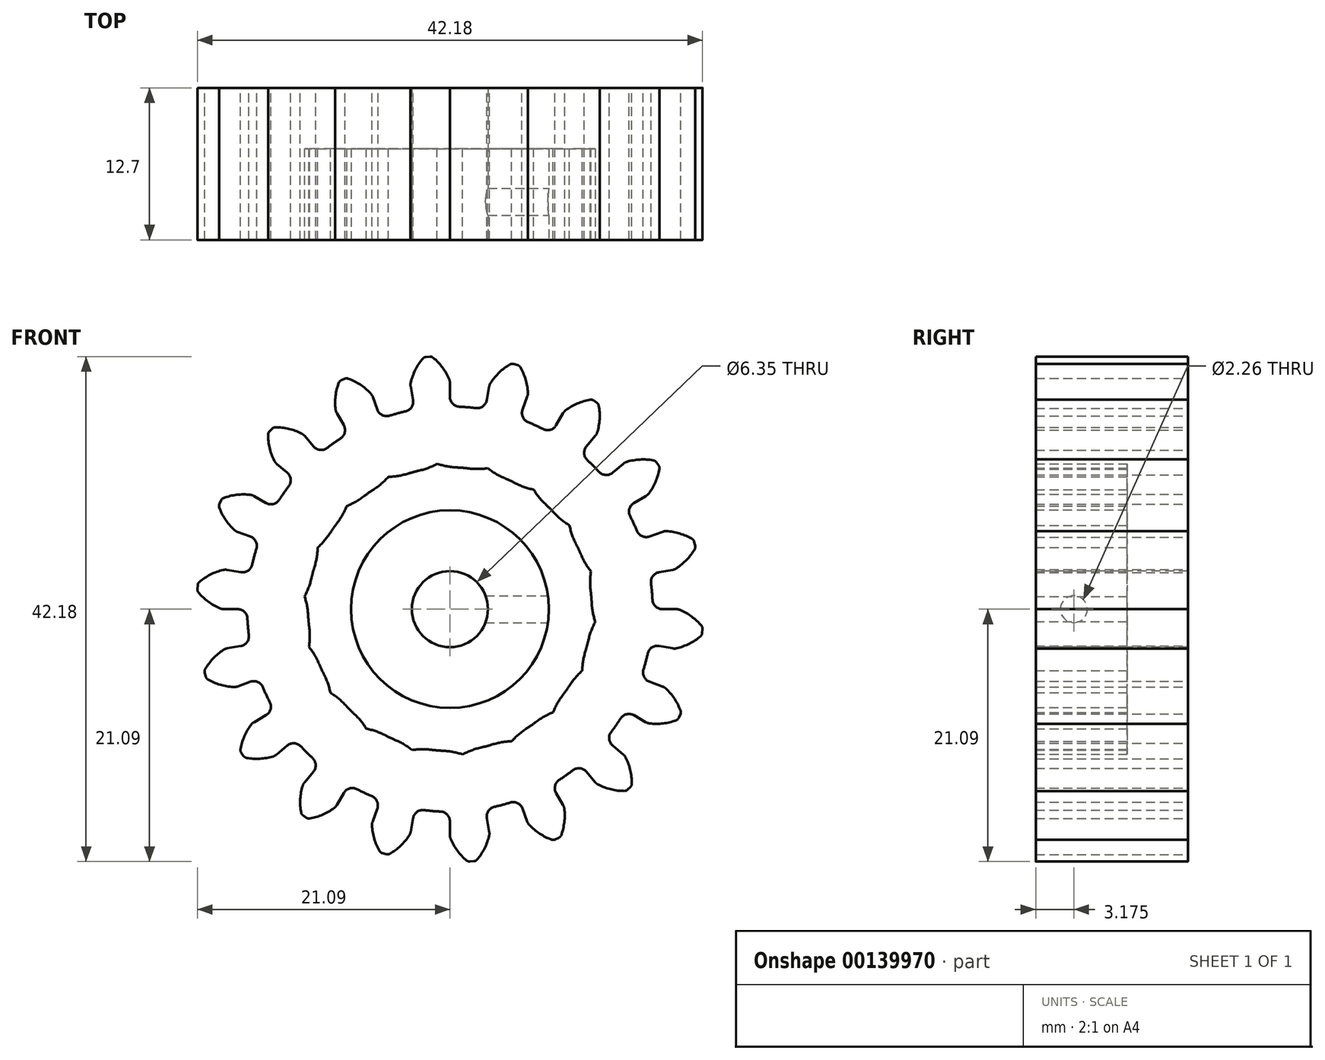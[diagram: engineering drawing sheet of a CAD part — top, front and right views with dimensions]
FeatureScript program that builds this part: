
annotation { "Feature Type Name" : "Feature", "Feature Type Description" : "" }
export const myFeature = defineFeature(function(context is Context, id is Id, definition is map)
    precondition{}
    {
        {
            var Q0;
            Q0=qCreatedBy(makeId("Front.planeOp"),FACE);
            var sketch = newSketch(context, id + "F0", { "sketchPlane" : qUnion([Q0])});
            skArc(sketch, "E0", {"start": v(-3.71, 16.52) * mm, "mid": v(-4.38, 16.35) * mm, "end": v(-5.04, 16.16) * mm});
            skArc(sketch, "E1.trimOffspring", {"start": v(-0.07, 19.21) * mm, "mid": v(-0.63, 20.19) * mm, "end": v(-1.4, 21) * mm});
            skLineSegment(sketch, "E2", {"start": v(-1.68, 21.09) * mm, "end": v(-1.84, 21.08) * mm});
            skLineSegment(sketch, "E3", {"start": v(0, 18.89) * mm, "end": v(0, 17.74) * mm});
            skLineSegment(sketch, "E4.MirrorCS", {"start": v(-2, 21.06) * mm, "end": v(-1.84, 21.08) * mm});
            skArc(sketch, "E5.MirrorCS", {"start": v(-3.27, 18.93) * mm, "mid": v(-2.89, 20) * mm, "end": v(-2.27, 20.93) * mm});
            skLineSegment(sketch, "E6.MirrorCS", {"start": v(-3.28, 18.6) * mm, "end": v(-3.08, 17.47) * mm});
            skPoint(sketch, "E7.visualSharp", {"position": v(0, 16.93) * mm});
            skArc(sketch, "E7.filletArc", {"start": v(0, 17.74) * mm, "mid": v(0.23, 17.17) * mm, "end": v(0.79, 16.91) * mm});
            skPoint(sketch, "E8.visualSharp", {"position": v(-2.94, 16.67) * mm});
            skArc(sketch, "E8.filletArc", {"start": v(-3.71, 16.52) * mm, "mid": v(-3.2, 16.86) * mm, "end": v(-3.08, 17.47) * mm});
            skPoint(sketch, "E9.visualSharp", {"position": v(-3.3, 18.76) * mm});
            skArc(sketch, "E9.filletArc", {"start": v(-3.27, 18.93) * mm, "mid": v(-3.3, 18.77) * mm, "end": v(-3.28, 18.6) * mm});
            skPoint(sketch, "E10.visualSharp", {"position": v(0, 19.05) * mm});
            skArc(sketch, "E10.filletArc", {"start": v(0, 18.89) * mm, "mid": v(-0.02, 19.05) * mm, "end": v(-0.07, 19.21) * mm});
            skPoint(sketch, "E11.visualSharp", {"position": v(-2.16, 21.05) * mm});
            skArc(sketch, "E11.filletArc", {"start": v(-2, 21.06) * mm, "mid": v(-2.15, 21.02) * mm, "end": v(-2.27, 20.93) * mm});
            skPoint(sketch, "E12.visualSharp", {"position": v(-1.53, 21.1) * mm});
            skArc(sketch, "E12.filletArc", {"start": v(-1.4, 21) * mm, "mid": v(-1.53, 21.07) * mm, "end": v(-1.68, 21.09) * mm});
            skArc(sketch, "E13.1.0", {"start": v(-9.14, 14.25) * mm, "mid": v(-8.78, 14.75) * mm, "end": v(-8.87, 15.36) * mm});
            skLineSegment(sketch, "E13.1.1", {"start": v(-9.44, 16.36) * mm, "end": v(-8.87, 15.36) * mm});
            skArc(sketch, "E13.1.2", {"start": v(-9.55, 16.67) * mm, "mid": v(-9.51, 16.51) * mm, "end": v(-9.44, 16.36) * mm});
            skArc(sketch, "E13.1.3", {"start": v(-9.55, 16.67) * mm, "mid": v(-9.55, 17.8) * mm, "end": v(-9.29, 18.89) * mm});
            skArc(sketch, "E13.1.4", {"start": v(-9.1, 19.1) * mm, "mid": v(-9.21, 19.02) * mm, "end": v(-9.29, 18.89) * mm});
            skLineSegment(sketch, "E13.1.5", {"start": v(-9.1, 19.1) * mm, "end": v(-8.94, 19.17) * mm});
            skLineSegment(sketch, "E13.1.6", {"start": v(-8.79, 19.24) * mm, "end": v(-8.94, 19.17) * mm});
            skArc(sketch, "E13.1.7", {"start": v(-8.5, 19.26) * mm, "mid": v(-8.65, 19.28) * mm, "end": v(-8.79, 19.24) * mm});
            skArc(sketch, "E13.1.8", {"start": v(-6.63, 18.03) * mm, "mid": v(-7.5, 18.76) * mm, "end": v(-8.5, 19.26) * mm});
            skArc(sketch, "E13.1.9", {"start": v(-6.46, 17.75) * mm, "mid": v(-6.53, 17.9) * mm, "end": v(-6.63, 18.03) * mm});
            skLineSegment(sketch, "E13.1.10", {"start": v(-6.46, 17.75) * mm, "end": v(-6.07, 16.67) * mm});
            skArc(sketch, "E13.1.11", {"start": v(-6.07, 16.67) * mm, "mid": v(-5.66, 16.2) * mm, "end": v(-5.04, 16.16) * mm});
            skArc(sketch, "E13.2.0", {"start": v(-13.46, 10.27) * mm, "mid": v(-13.3, 10.86) * mm, "end": v(-13.59, 11.4) * mm});
            skLineSegment(sketch, "E13.2.1", {"start": v(-14.47, 12.14) * mm, "end": v(-13.59, 11.4) * mm});
            skArc(sketch, "E13.2.2", {"start": v(-14.68, 12.4) * mm, "mid": v(-14.59, 12.26) * mm, "end": v(-14.47, 12.14) * mm});
            skArc(sketch, "E13.2.3", {"start": v(-14.68, 12.4) * mm, "mid": v(-15.06, 13.46) * mm, "end": v(-15.19, 14.57) * mm});
            skArc(sketch, "E13.2.4", {"start": v(-15.08, 14.84) * mm, "mid": v(-15.16, 14.72) * mm, "end": v(-15.19, 14.57) * mm});
            skLineSegment(sketch, "E13.2.5", {"start": v(-15.08, 14.84) * mm, "end": v(-14.96, 14.96) * mm});
            skLineSegment(sketch, "E13.2.6", {"start": v(-14.84, 15.08) * mm, "end": v(-14.96, 14.96) * mm});
            skArc(sketch, "E13.2.7", {"start": v(-14.57, 15.19) * mm, "mid": v(-14.72, 15.16) * mm, "end": v(-14.84, 15.08) * mm});
            skArc(sketch, "E13.2.8", {"start": v(-12.4, 14.68) * mm, "mid": v(-13.46, 15.06) * mm, "end": v(-14.57, 15.19) * mm});
            skArc(sketch, "E13.2.9", {"start": v(-12.14, 14.47) * mm, "mid": v(-12.26, 14.59) * mm, "end": v(-12.4, 14.68) * mm});
            skLineSegment(sketch, "E13.2.10", {"start": v(-12.14, 14.47) * mm, "end": v(-11.4, 13.59) * mm});
            skArc(sketch, "E13.2.11", {"start": v(-11.4, 13.59) * mm, "mid": v(-10.86, 13.3) * mm, "end": v(-10.27, 13.46) * mm});
            skArc(sketch, "E13.3.0", {"start": v(-16.16, 5.04) * mm, "mid": v(-16.2, 5.66) * mm, "end": v(-16.67, 6.07) * mm});
            skLineSegment(sketch, "E13.3.1", {"start": v(-17.75, 6.46) * mm, "end": v(-16.67, 6.07) * mm});
            skArc(sketch, "E13.3.2", {"start": v(-18.03, 6.63) * mm, "mid": v(-17.9, 6.53) * mm, "end": v(-17.75, 6.46) * mm});
            skArc(sketch, "E13.3.3", {"start": v(-18.03, 6.63) * mm, "mid": v(-18.76, 7.5) * mm, "end": v(-19.26, 8.5) * mm});
            skArc(sketch, "E13.3.4", {"start": v(-19.24, 8.79) * mm, "mid": v(-19.28, 8.65) * mm, "end": v(-19.26, 8.5) * mm});
            skLineSegment(sketch, "E13.3.5", {"start": v(-19.24, 8.79) * mm, "end": v(-19.17, 8.94) * mm});
            skLineSegment(sketch, "E13.3.6", {"start": v(-19.1, 9.1) * mm, "end": v(-19.17, 8.94) * mm});
            skArc(sketch, "E13.3.7", {"start": v(-18.89, 9.29) * mm, "mid": v(-19.02, 9.21) * mm, "end": v(-19.1, 9.1) * mm});
            skArc(sketch, "E13.3.8", {"start": v(-16.67, 9.55) * mm, "mid": v(-17.8, 9.55) * mm, "end": v(-18.89, 9.29) * mm});
            skArc(sketch, "E13.3.9", {"start": v(-16.36, 9.44) * mm, "mid": v(-16.51, 9.51) * mm, "end": v(-16.67, 9.55) * mm});
            skLineSegment(sketch, "E13.3.10", {"start": v(-16.36, 9.44) * mm, "end": v(-15.36, 8.87) * mm});
            skArc(sketch, "E13.3.11", {"start": v(-15.36, 8.87) * mm, "mid": v(-14.75, 8.78) * mm, "end": v(-14.25, 9.14) * mm});
            skArc(sketch, "E13.4.0", {"start": v(-16.91, -0.79) * mm, "mid": v(-17.17, -0.23) * mm, "end": v(-17.74, 0) * mm});
            skLineSegment(sketch, "E13.4.1", {"start": v(-18.89, 0) * mm, "end": v(-17.74, 0) * mm});
            skArc(sketch, "E13.4.2", {"start": v(-19.21, 0.07) * mm, "mid": v(-19.05, 0.02) * mm, "end": v(-18.89, 0) * mm});
            skArc(sketch, "E13.4.3", {"start": v(-19.21, 0.07) * mm, "mid": v(-20.19, 0.63) * mm, "end": v(-21, 1.4) * mm});
            skArc(sketch, "E13.4.4", {"start": v(-21.09, 1.68) * mm, "mid": v(-21.07, 1.53) * mm, "end": v(-21, 1.4) * mm});
            skLineSegment(sketch, "E13.4.5", {"start": v(-21.09, 1.68) * mm, "end": v(-21.08, 1.84) * mm});
            skLineSegment(sketch, "E13.4.6", {"start": v(-21.06, 2) * mm, "end": v(-21.08, 1.84) * mm});
            skArc(sketch, "E13.4.7", {"start": v(-20.93, 2.27) * mm, "mid": v(-21.02, 2.15) * mm, "end": v(-21.06, 2) * mm});
            skArc(sketch, "E13.4.8", {"start": v(-18.93, 3.27) * mm, "mid": v(-20, 2.89) * mm, "end": v(-20.93, 2.27) * mm});
            skArc(sketch, "E13.4.9", {"start": v(-18.6, 3.28) * mm, "mid": v(-18.77, 3.3) * mm, "end": v(-18.93, 3.27) * mm});
            skLineSegment(sketch, "E13.4.10", {"start": v(-18.6, 3.28) * mm, "end": v(-17.47, 3.08) * mm});
            skArc(sketch, "E13.4.11", {"start": v(-17.47, 3.08) * mm, "mid": v(-16.86, 3.2) * mm, "end": v(-16.52, 3.71) * mm});
            skArc(sketch, "E13.5.0", {"start": v(-15.62, -6.52) * mm, "mid": v(-16.05, -6.09) * mm, "end": v(-16.67, -6.07) * mm});
            skLineSegment(sketch, "E13.5.1", {"start": v(-17.75, -6.46) * mm, "end": v(-16.67, -6.07) * mm});
            skArc(sketch, "E13.5.2", {"start": v(-18.08, -6.5) * mm, "mid": v(-17.91, -6.5) * mm, "end": v(-17.75, -6.46) * mm});
            skArc(sketch, "E13.5.3", {"start": v(-18.08, -6.5) * mm, "mid": v(-19.19, -6.31) * mm, "end": v(-20.22, -5.87) * mm});
            skArc(sketch, "E13.5.4", {"start": v(-20.4, -5.64) * mm, "mid": v(-20.33, -5.77) * mm, "end": v(-20.22, -5.87) * mm});
            skLineSegment(sketch, "E13.5.5", {"start": v(-20.4, -5.64) * mm, "end": v(-20.43, -5.48) * mm});
            skLineSegment(sketch, "E13.5.6", {"start": v(-20.48, -5.31) * mm, "end": v(-20.43, -5.48) * mm});
            skArc(sketch, "E13.5.7", {"start": v(-20.44, -5.03) * mm, "mid": v(-20.49, -5.17) * mm, "end": v(-20.48, -5.31) * mm});
            skArc(sketch, "E13.5.8", {"start": v(-18.91, -3.4) * mm, "mid": v(-19.77, -4.12) * mm, "end": v(-20.44, -5.03) * mm});
            skArc(sketch, "E13.5.9", {"start": v(-18.6, -3.28) * mm, "mid": v(-18.76, -3.33) * mm, "end": v(-18.91, -3.4) * mm});
            skLineSegment(sketch, "E13.5.10", {"start": v(-18.6, -3.28) * mm, "end": v(-17.47, -3.08) * mm});
            skArc(sketch, "E13.5.11", {"start": v(-17.47, -3.08) * mm, "mid": v(-16.94, -2.76) * mm, "end": v(-16.8, -2.16) * mm});
            skArc(sketch, "E13.6.0", {"start": v(-12.45, -11.47) * mm, "mid": v(-13, -11.2) * mm, "end": v(-13.59, -11.4) * mm});
            skLineSegment(sketch, "E13.6.1", {"start": v(-14.47, -12.14) * mm, "end": v(-13.59, -11.4) * mm});
            skArc(sketch, "E13.6.2", {"start": v(-14.76, -12.3) * mm, "mid": v(-14.6, -12.24) * mm, "end": v(-14.47, -12.14) * mm});
            skArc(sketch, "E13.6.3", {"start": v(-14.76, -12.3) * mm, "mid": v(-15.87, -12.5) * mm, "end": v(-17, -12.43) * mm});
            skArc(sketch, "E13.6.4", {"start": v(-17.23, -12.27) * mm, "mid": v(-17.13, -12.37) * mm, "end": v(-17, -12.43) * mm});
            skLineSegment(sketch, "E13.6.5", {"start": v(-17.23, -12.27) * mm, "end": v(-17.33, -12.13) * mm});
            skLineSegment(sketch, "E13.6.6", {"start": v(-17.43, -12) * mm, "end": v(-17.33, -12.13) * mm});
            skArc(sketch, "E13.6.7", {"start": v(-17.49, -11.72) * mm, "mid": v(-17.49, -11.86) * mm, "end": v(-17.43, -12) * mm});
            skArc(sketch, "E13.6.8", {"start": v(-16.6, -9.66) * mm, "mid": v(-17.17, -10.64) * mm, "end": v(-17.49, -11.72) * mm});
            skArc(sketch, "E13.6.9", {"start": v(-16.36, -9.44) * mm, "mid": v(-16.5, -9.54) * mm, "end": v(-16.6, -9.66) * mm});
            skLineSegment(sketch, "E13.6.10", {"start": v(-16.36, -9.44) * mm, "end": v(-15.36, -8.87) * mm});
            skArc(sketch, "E13.6.11", {"start": v(-15.36, -8.87) * mm, "mid": v(-14.98, -8.38) * mm, "end": v(-15.04, -7.77) * mm});
            skArc(sketch, "E13.7.0", {"start": v(-7.77, -15.04) * mm, "mid": v(-8.38, -14.98) * mm, "end": v(-8.87, -15.36) * mm});
            skLineSegment(sketch, "E13.7.1", {"start": v(-9.44, -16.36) * mm, "end": v(-8.87, -15.36) * mm});
            skArc(sketch, "E13.7.2", {"start": v(-9.66, -16.6) * mm, "mid": v(-9.54, -16.5) * mm, "end": v(-9.44, -16.36) * mm});
            skArc(sketch, "E13.7.3", {"start": v(-9.66, -16.6) * mm, "mid": v(-10.64, -17.17) * mm, "end": v(-11.72, -17.49) * mm});
            skArc(sketch, "E13.7.4", {"start": v(-12, -17.43) * mm, "mid": v(-11.86, -17.49) * mm, "end": v(-11.72, -17.49) * mm});
            skLineSegment(sketch, "E13.7.5", {"start": v(-12, -17.43) * mm, "end": v(-12.13, -17.33) * mm});
            skLineSegment(sketch, "E13.7.6", {"start": v(-12.27, -17.23) * mm, "end": v(-12.13, -17.33) * mm});
            skArc(sketch, "E13.7.7", {"start": v(-12.43, -17) * mm, "mid": v(-12.37, -17.13) * mm, "end": v(-12.27, -17.23) * mm});
            skArc(sketch, "E13.7.8", {"start": v(-12.3, -14.76) * mm, "mid": v(-12.5, -15.87) * mm, "end": v(-12.43, -17) * mm});
            skArc(sketch, "E13.7.9", {"start": v(-12.14, -14.47) * mm, "mid": v(-12.24, -14.6) * mm, "end": v(-12.3, -14.76) * mm});
            skLineSegment(sketch, "E13.7.10", {"start": v(-12.14, -14.47) * mm, "end": v(-11.4, -13.59) * mm});
            skArc(sketch, "E13.7.11", {"start": v(-11.4, -13.59) * mm, "mid": v(-11.2, -13) * mm, "end": v(-11.47, -12.45) * mm});
            skArc(sketch, "E13.8.0", {"start": v(-2.16, -16.8) * mm, "mid": v(-2.76, -16.94) * mm, "end": v(-3.08, -17.47) * mm});
            skLineSegment(sketch, "E13.8.1", {"start": v(-3.28, -18.6) * mm, "end": v(-3.08, -17.47) * mm});
            skArc(sketch, "E13.8.2", {"start": v(-3.4, -18.91) * mm, "mid": v(-3.33, -18.76) * mm, "end": v(-3.28, -18.6) * mm});
            skArc(sketch, "E13.8.3", {"start": v(-3.4, -18.91) * mm, "mid": v(-4.12, -19.77) * mm, "end": v(-5.03, -20.44) * mm});
            skArc(sketch, "E13.8.4", {"start": v(-5.31, -20.48) * mm, "mid": v(-5.17, -20.49) * mm, "end": v(-5.03, -20.44) * mm});
            skLineSegment(sketch, "E13.8.5", {"start": v(-5.31, -20.48) * mm, "end": v(-5.48, -20.43) * mm});
            skLineSegment(sketch, "E13.8.6", {"start": v(-5.64, -20.4) * mm, "end": v(-5.48, -20.43) * mm});
            skArc(sketch, "E13.8.7", {"start": v(-5.87, -20.22) * mm, "mid": v(-5.77, -20.33) * mm, "end": v(-5.64, -20.4) * mm});
            skArc(sketch, "E13.8.8", {"start": v(-6.5, -18.08) * mm, "mid": v(-6.31, -19.19) * mm, "end": v(-5.87, -20.22) * mm});
            skArc(sketch, "E13.8.9", {"start": v(-6.46, -17.75) * mm, "mid": v(-6.5, -17.91) * mm, "end": v(-6.5, -18.08) * mm});
            skLineSegment(sketch, "E13.8.10", {"start": v(-6.46, -17.75) * mm, "end": v(-6.07, -16.67) * mm});
            skArc(sketch, "E13.8.11", {"start": v(-6.07, -16.67) * mm, "mid": v(-6.09, -16.05) * mm, "end": v(-6.52, -15.62) * mm});
            skArc(sketch, "E13.9.0", {"start": v(3.71, -16.52) * mm, "mid": v(3.2, -16.86) * mm, "end": v(3.08, -17.47) * mm});
            skLineSegment(sketch, "E13.9.1", {"start": v(3.28, -18.6) * mm, "end": v(3.08, -17.47) * mm});
            skArc(sketch, "E13.9.2", {"start": v(3.27, -18.93) * mm, "mid": v(3.3, -18.77) * mm, "end": v(3.28, -18.6) * mm});
            skArc(sketch, "E13.9.3", {"start": v(3.27, -18.93) * mm, "mid": v(2.89, -20) * mm, "end": v(2.27, -20.93) * mm});
            skArc(sketch, "E13.9.4", {"start": v(2, -21.06) * mm, "mid": v(2.15, -21.02) * mm, "end": v(2.27, -20.93) * mm});
            skLineSegment(sketch, "E13.9.5", {"start": v(2, -21.06) * mm, "end": v(1.84, -21.08) * mm});
            skLineSegment(sketch, "E13.9.6", {"start": v(1.68, -21.09) * mm, "end": v(1.84, -21.08) * mm});
            skArc(sketch, "E13.9.7", {"start": v(1.4, -21) * mm, "mid": v(1.53, -21.07) * mm, "end": v(1.68, -21.09) * mm});
            skArc(sketch, "E13.9.8", {"start": v(0.07, -19.21) * mm, "mid": v(0.63, -20.19) * mm, "end": v(1.4, -21) * mm});
            skArc(sketch, "E13.9.9", {"start": v(0, -18.89) * mm, "mid": v(0.02, -19.05) * mm, "end": v(0.07, -19.21) * mm});
            skLineSegment(sketch, "E13.9.10", {"start": v(0, -18.89) * mm, "end": v(0, -17.74) * mm});
            skArc(sketch, "E13.9.11", {"start": v(0, -17.74) * mm, "mid": v(-0.23, -17.17) * mm, "end": v(-0.79, -16.91) * mm});
            skArc(sketch, "E13.10.0", {"start": v(9.14, -14.25) * mm, "mid": v(8.78, -14.75) * mm, "end": v(8.87, -15.36) * mm});
            skLineSegment(sketch, "E13.10.1", {"start": v(9.44, -16.36) * mm, "end": v(8.87, -15.36) * mm});
            skArc(sketch, "E13.10.2", {"start": v(9.55, -16.67) * mm, "mid": v(9.51, -16.51) * mm, "end": v(9.44, -16.36) * mm});
            skArc(sketch, "E13.10.3", {"start": v(9.55, -16.67) * mm, "mid": v(9.55, -17.8) * mm, "end": v(9.29, -18.89) * mm});
            skArc(sketch, "E13.10.4", {"start": v(9.1, -19.1) * mm, "mid": v(9.21, -19.02) * mm, "end": v(9.29, -18.89) * mm});
            skLineSegment(sketch, "E13.10.5", {"start": v(9.1, -19.1) * mm, "end": v(8.94, -19.17) * mm});
            skLineSegment(sketch, "E13.10.6", {"start": v(8.79, -19.24) * mm, "end": v(8.94, -19.17) * mm});
            skArc(sketch, "E13.10.7", {"start": v(8.5, -19.26) * mm, "mid": v(8.65, -19.28) * mm, "end": v(8.79, -19.24) * mm});
            skArc(sketch, "E13.10.8", {"start": v(6.63, -18.03) * mm, "mid": v(7.5, -18.76) * mm, "end": v(8.5, -19.26) * mm});
            skArc(sketch, "E13.10.9", {"start": v(6.46, -17.75) * mm, "mid": v(6.53, -17.9) * mm, "end": v(6.63, -18.03) * mm});
            skLineSegment(sketch, "E13.10.10", {"start": v(6.46, -17.75) * mm, "end": v(6.07, -16.67) * mm});
            skArc(sketch, "E13.10.11", {"start": v(6.07, -16.67) * mm, "mid": v(5.66, -16.2) * mm, "end": v(5.04, -16.16) * mm});
            skArc(sketch, "E13.11.0", {"start": v(13.46, -10.27) * mm, "mid": v(13.3, -10.86) * mm, "end": v(13.59, -11.4) * mm});
            skLineSegment(sketch, "E13.11.1", {"start": v(14.47, -12.14) * mm, "end": v(13.59, -11.4) * mm});
            skArc(sketch, "E13.11.2", {"start": v(14.68, -12.4) * mm, "mid": v(14.59, -12.26) * mm, "end": v(14.47, -12.14) * mm});
            skArc(sketch, "E13.11.3", {"start": v(14.68, -12.4) * mm, "mid": v(15.06, -13.46) * mm, "end": v(15.19, -14.57) * mm});
            skArc(sketch, "E13.11.4", {"start": v(15.08, -14.84) * mm, "mid": v(15.16, -14.72) * mm, "end": v(15.19, -14.57) * mm});
            skLineSegment(sketch, "E13.11.5", {"start": v(15.08, -14.84) * mm, "end": v(14.96, -14.96) * mm});
            skLineSegment(sketch, "E13.11.6", {"start": v(14.84, -15.08) * mm, "end": v(14.96, -14.96) * mm});
            skArc(sketch, "E13.11.7", {"start": v(14.57, -15.19) * mm, "mid": v(14.72, -15.16) * mm, "end": v(14.84, -15.08) * mm});
            skArc(sketch, "E13.11.8", {"start": v(12.4, -14.68) * mm, "mid": v(13.46, -15.06) * mm, "end": v(14.57, -15.19) * mm});
            skArc(sketch, "E13.11.9", {"start": v(12.14, -14.47) * mm, "mid": v(12.26, -14.59) * mm, "end": v(12.4, -14.68) * mm});
            skLineSegment(sketch, "E13.11.10", {"start": v(12.14, -14.47) * mm, "end": v(11.4, -13.59) * mm});
            skArc(sketch, "E13.11.11", {"start": v(11.4, -13.59) * mm, "mid": v(10.86, -13.3) * mm, "end": v(10.27, -13.46) * mm});
            skArc(sketch, "E13.12.0", {"start": v(16.16, -5.04) * mm, "mid": v(16.2, -5.66) * mm, "end": v(16.67, -6.07) * mm});
            skLineSegment(sketch, "E13.12.1", {"start": v(17.75, -6.46) * mm, "end": v(16.67, -6.07) * mm});
            skArc(sketch, "E13.12.2", {"start": v(18.03, -6.63) * mm, "mid": v(17.9, -6.53) * mm, "end": v(17.75, -6.46) * mm});
            skArc(sketch, "E13.12.3", {"start": v(18.03, -6.63) * mm, "mid": v(18.76, -7.5) * mm, "end": v(19.26, -8.5) * mm});
            skArc(sketch, "E13.12.4", {"start": v(19.24, -8.79) * mm, "mid": v(19.28, -8.65) * mm, "end": v(19.26, -8.5) * mm});
            skLineSegment(sketch, "E13.12.5", {"start": v(19.24, -8.79) * mm, "end": v(19.17, -8.94) * mm});
            skLineSegment(sketch, "E13.12.6", {"start": v(19.1, -9.1) * mm, "end": v(19.17, -8.94) * mm});
            skArc(sketch, "E13.12.7", {"start": v(18.89, -9.29) * mm, "mid": v(19.02, -9.21) * mm, "end": v(19.1, -9.1) * mm});
            skArc(sketch, "E13.12.8", {"start": v(16.67, -9.55) * mm, "mid": v(17.8, -9.55) * mm, "end": v(18.89, -9.29) * mm});
            skArc(sketch, "E13.12.9", {"start": v(16.36, -9.44) * mm, "mid": v(16.51, -9.51) * mm, "end": v(16.67, -9.55) * mm});
            skLineSegment(sketch, "E13.12.10", {"start": v(16.36, -9.44) * mm, "end": v(15.36, -8.87) * mm});
            skArc(sketch, "E13.12.11", {"start": v(15.36, -8.87) * mm, "mid": v(14.75, -8.78) * mm, "end": v(14.25, -9.14) * mm});
            skArc(sketch, "E13.13.0", {"start": v(16.91, 0.79) * mm, "mid": v(17.17, 0.23) * mm, "end": v(17.74, 0) * mm});
            skLineSegment(sketch, "E13.13.1", {"start": v(18.89, 0) * mm, "end": v(17.74, 0) * mm});
            skArc(sketch, "E13.13.2", {"start": v(19.21, -0.07) * mm, "mid": v(19.05, -0.02) * mm, "end": v(18.89, 0) * mm});
            skArc(sketch, "E13.13.3", {"start": v(19.21, -0.07) * mm, "mid": v(20.19, -0.63) * mm, "end": v(21, -1.4) * mm});
            skArc(sketch, "E13.13.4", {"start": v(21.09, -1.68) * mm, "mid": v(21.07, -1.53) * mm, "end": v(21, -1.4) * mm});
            skLineSegment(sketch, "E13.13.5", {"start": v(21.09, -1.68) * mm, "end": v(21.08, -1.84) * mm});
            skLineSegment(sketch, "E13.13.6", {"start": v(21.06, -2) * mm, "end": v(21.08, -1.84) * mm});
            skArc(sketch, "E13.13.7", {"start": v(20.93, -2.27) * mm, "mid": v(21.02, -2.15) * mm, "end": v(21.06, -2) * mm});
            skArc(sketch, "E13.13.8", {"start": v(18.93, -3.27) * mm, "mid": v(20, -2.89) * mm, "end": v(20.93, -2.27) * mm});
            skArc(sketch, "E13.13.9", {"start": v(18.6, -3.28) * mm, "mid": v(18.77, -3.3) * mm, "end": v(18.93, -3.27) * mm});
            skLineSegment(sketch, "E13.13.10", {"start": v(18.6, -3.28) * mm, "end": v(17.47, -3.08) * mm});
            skArc(sketch, "E13.13.11", {"start": v(17.47, -3.08) * mm, "mid": v(16.86, -3.2) * mm, "end": v(16.52, -3.71) * mm});
            skArc(sketch, "E13.14.0", {"start": v(15.62, 6.52) * mm, "mid": v(16.05, 6.09) * mm, "end": v(16.67, 6.07) * mm});
            skLineSegment(sketch, "E13.14.1", {"start": v(17.75, 6.46) * mm, "end": v(16.67, 6.07) * mm});
            skArc(sketch, "E13.14.2", {"start": v(18.08, 6.5) * mm, "mid": v(17.91, 6.5) * mm, "end": v(17.75, 6.46) * mm});
            skArc(sketch, "E13.14.3", {"start": v(18.08, 6.5) * mm, "mid": v(19.19, 6.31) * mm, "end": v(20.22, 5.87) * mm});
            skArc(sketch, "E13.14.4", {"start": v(20.4, 5.64) * mm, "mid": v(20.33, 5.77) * mm, "end": v(20.22, 5.87) * mm});
            skLineSegment(sketch, "E13.14.5", {"start": v(20.4, 5.64) * mm, "end": v(20.43, 5.48) * mm});
            skLineSegment(sketch, "E13.14.6", {"start": v(20.48, 5.31) * mm, "end": v(20.43, 5.48) * mm});
            skArc(sketch, "E13.14.7", {"start": v(20.44, 5.03) * mm, "mid": v(20.49, 5.17) * mm, "end": v(20.48, 5.31) * mm});
            skArc(sketch, "E13.14.8", {"start": v(18.91, 3.4) * mm, "mid": v(19.77, 4.12) * mm, "end": v(20.44, 5.03) * mm});
            skArc(sketch, "E13.14.9", {"start": v(18.6, 3.28) * mm, "mid": v(18.76, 3.33) * mm, "end": v(18.91, 3.4) * mm});
            skLineSegment(sketch, "E13.14.10", {"start": v(18.6, 3.28) * mm, "end": v(17.47, 3.08) * mm});
            skArc(sketch, "E13.14.11", {"start": v(17.47, 3.08) * mm, "mid": v(16.94, 2.76) * mm, "end": v(16.8, 2.16) * mm});
            skArc(sketch, "E13.15.0", {"start": v(12.45, 11.47) * mm, "mid": v(13, 11.2) * mm, "end": v(13.59, 11.4) * mm});
            skLineSegment(sketch, "E13.15.1", {"start": v(14.47, 12.14) * mm, "end": v(13.59, 11.4) * mm});
            skArc(sketch, "E13.15.2", {"start": v(14.76, 12.3) * mm, "mid": v(14.6, 12.24) * mm, "end": v(14.47, 12.14) * mm});
            skArc(sketch, "E13.15.3", {"start": v(14.76, 12.3) * mm, "mid": v(15.87, 12.5) * mm, "end": v(17, 12.43) * mm});
            skArc(sketch, "E13.15.4", {"start": v(17.23, 12.27) * mm, "mid": v(17.13, 12.37) * mm, "end": v(17, 12.43) * mm});
            skLineSegment(sketch, "E13.15.5", {"start": v(17.23, 12.27) * mm, "end": v(17.33, 12.13) * mm});
            skLineSegment(sketch, "E13.15.6", {"start": v(17.43, 12) * mm, "end": v(17.33, 12.13) * mm});
            skArc(sketch, "E13.15.7", {"start": v(17.49, 11.72) * mm, "mid": v(17.49, 11.86) * mm, "end": v(17.43, 12) * mm});
            skArc(sketch, "E13.15.8", {"start": v(16.6, 9.66) * mm, "mid": v(17.17, 10.64) * mm, "end": v(17.49, 11.72) * mm});
            skArc(sketch, "E13.15.9", {"start": v(16.36, 9.44) * mm, "mid": v(16.5, 9.54) * mm, "end": v(16.6, 9.66) * mm});
            skLineSegment(sketch, "E13.15.10", {"start": v(16.36, 9.44) * mm, "end": v(15.36, 8.87) * mm});
            skArc(sketch, "E13.15.11", {"start": v(15.36, 8.87) * mm, "mid": v(14.98, 8.38) * mm, "end": v(15.04, 7.77) * mm});
            skArc(sketch, "E13.16.0", {"start": v(7.77, 15.04) * mm, "mid": v(8.38, 14.98) * mm, "end": v(8.87, 15.36) * mm});
            skLineSegment(sketch, "E13.16.1", {"start": v(9.44, 16.36) * mm, "end": v(8.87, 15.36) * mm});
            skArc(sketch, "E13.16.2", {"start": v(9.66, 16.6) * mm, "mid": v(9.54, 16.5) * mm, "end": v(9.44, 16.36) * mm});
            skArc(sketch, "E13.16.3", {"start": v(9.66, 16.6) * mm, "mid": v(10.64, 17.17) * mm, "end": v(11.72, 17.49) * mm});
            skArc(sketch, "E13.16.4", {"start": v(12, 17.43) * mm, "mid": v(11.86, 17.49) * mm, "end": v(11.72, 17.49) * mm});
            skLineSegment(sketch, "E13.16.5", {"start": v(12, 17.43) * mm, "end": v(12.13, 17.33) * mm});
            skLineSegment(sketch, "E13.16.6", {"start": v(12.27, 17.23) * mm, "end": v(12.13, 17.33) * mm});
            skArc(sketch, "E13.16.7", {"start": v(12.43, 17) * mm, "mid": v(12.37, 17.13) * mm, "end": v(12.27, 17.23) * mm});
            skArc(sketch, "E13.16.8", {"start": v(12.3, 14.76) * mm, "mid": v(12.5, 15.87) * mm, "end": v(12.43, 17) * mm});
            skArc(sketch, "E13.16.9", {"start": v(12.14, 14.47) * mm, "mid": v(12.24, 14.6) * mm, "end": v(12.3, 14.76) * mm});
            skLineSegment(sketch, "E13.16.10", {"start": v(12.14, 14.47) * mm, "end": v(11.4, 13.59) * mm});
            skArc(sketch, "E13.16.11", {"start": v(11.4, 13.59) * mm, "mid": v(11.2, 13) * mm, "end": v(11.47, 12.45) * mm});
            skArc(sketch, "E13.17.0", {"start": v(2.16, 16.8) * mm, "mid": v(2.76, 16.94) * mm, "end": v(3.08, 17.47) * mm});
            skLineSegment(sketch, "E13.17.1", {"start": v(3.28, 18.6) * mm, "end": v(3.08, 17.47) * mm});
            skArc(sketch, "E13.17.2", {"start": v(3.4, 18.91) * mm, "mid": v(3.33, 18.76) * mm, "end": v(3.28, 18.6) * mm});
            skArc(sketch, "E13.17.3", {"start": v(3.4, 18.91) * mm, "mid": v(4.12, 19.77) * mm, "end": v(5.03, 20.44) * mm});
            skArc(sketch, "E13.17.4", {"start": v(5.31, 20.48) * mm, "mid": v(5.17, 20.49) * mm, "end": v(5.03, 20.44) * mm});
            skLineSegment(sketch, "E13.17.5", {"start": v(5.31, 20.48) * mm, "end": v(5.48, 20.43) * mm});
            skLineSegment(sketch, "E13.17.6", {"start": v(5.64, 20.4) * mm, "end": v(5.48, 20.43) * mm});
            skArc(sketch, "E13.17.7", {"start": v(5.87, 20.22) * mm, "mid": v(5.77, 20.33) * mm, "end": v(5.64, 20.4) * mm});
            skArc(sketch, "E13.17.8", {"start": v(6.5, 18.08) * mm, "mid": v(6.31, 19.19) * mm, "end": v(5.87, 20.22) * mm});
            skArc(sketch, "E13.17.9", {"start": v(6.46, 17.75) * mm, "mid": v(6.5, 17.91) * mm, "end": v(6.5, 18.08) * mm});
            skLineSegment(sketch, "E13.17.10", {"start": v(6.46, 17.75) * mm, "end": v(6.07, 16.67) * mm});
            skArc(sketch, "E13.17.11", {"start": v(6.07, 16.67) * mm, "mid": v(6.09, 16.05) * mm, "end": v(6.52, 15.62) * mm});
            skArc(sketch, "E14.trimOffspring", {"start": v(-13.46, 10.27) * mm, "mid": v(-13.87, 9.71) * mm, "end": v(-14.25, 9.14) * mm});
            skArc(sketch, "E15.trimOffspring", {"start": v(-9.14, 14.25) * mm, "mid": v(-9.71, 13.87) * mm, "end": v(-10.27, 13.46) * mm});
            skArc(sketch, "E16.trimOffspring", {"start": v(-16.16, 5.04) * mm, "mid": v(-16.35, 4.38) * mm, "end": v(-16.52, 3.71) * mm});
            skArc(sketch, "E17.trimOffspring", {"start": v(-16.91, -0.79) * mm, "mid": v(-16.86, -1.48) * mm, "end": v(-16.8, -2.16) * mm});
            skArc(sketch, "E18.trimOffspring", {"start": v(2.16, 16.8) * mm, "mid": v(1.48, 16.86) * mm, "end": v(0.79, 16.91) * mm});
            skArc(sketch, "E19.trimOffspring", {"start": v(7.77, 15.04) * mm, "mid": v(7.15, 15.34) * mm, "end": v(6.52, 15.62) * mm});
            skArc(sketch, "E20.trimOffspring", {"start": v(12.45, 11.47) * mm, "mid": v(11.97, 11.97) * mm, "end": v(11.47, 12.45) * mm});
            skArc(sketch, "E21.trimOffspring", {"start": v(15.62, 6.52) * mm, "mid": v(15.34, 7.15) * mm, "end": v(15.04, 7.77) * mm});
            skArc(sketch, "E22.trimOffspring", {"start": v(-2.16, -16.8) * mm, "mid": v(-1.48, -16.86) * mm, "end": v(-0.79, -16.91) * mm});
            skArc(sketch, "E23.trimOffspring", {"start": v(-7.77, -15.04) * mm, "mid": v(-7.15, -15.34) * mm, "end": v(-6.52, -15.62) * mm});
            skArc(sketch, "E24.trimOffspring", {"start": v(-12.45, -11.47) * mm, "mid": v(-11.97, -11.97) * mm, "end": v(-11.47, -12.45) * mm});
            skArc(sketch, "E25.trimOffspring", {"start": v(-15.62, -6.52) * mm, "mid": v(-15.34, -7.15) * mm, "end": v(-15.04, -7.77) * mm});
            skArc(sketch, "E26.trimOffspring", {"start": v(3.71, -16.52) * mm, "mid": v(4.38, -16.35) * mm, "end": v(5.04, -16.16) * mm});
            skArc(sketch, "E27.trimOffspring", {"start": v(9.14, -14.25) * mm, "mid": v(9.71, -13.87) * mm, "end": v(10.27, -13.46) * mm});
            skArc(sketch, "E28.trimOffspring", {"start": v(13.46, -10.27) * mm, "mid": v(13.87, -9.71) * mm, "end": v(14.25, -9.14) * mm});
            skArc(sketch, "E29.trimOffspring", {"start": v(16.16, -5.04) * mm, "mid": v(16.35, -4.38) * mm, "end": v(16.52, -3.71) * mm});
            skArc(sketch, "E30.trimOffspring", {"start": v(16.91, 0.79) * mm, "mid": v(16.86, 1.48) * mm, "end": v(16.8, 2.16) * mm});
            skSolve(sketch);
        }
        {
            var Q0;
            Q0 = qSketchRegion(id + "F0", true);
            extrude(context, id + "F1", {"entities" : qUnion([Q0]), "depth" : 12.7 * mm});
        }
        {
            var Q0;
            Q0=makeQuery(id+"F1.opExtrude","CAP_FACE",FACE,{"disambiguationData":[OSD([sQuery(id+"F0.wireOp",EDGE,"E0"),sQuery(id+"F0.wireOp",EDGE,"E1.trimOffspring"),sQuery(id+"F0.wireOp",EDGE,"E2"),sQuery(id+"F0.wireOp",EDGE,"E3"),sQuery(id+"F0.wireOp",EDGE,"E4.MirrorCS"),sQuery(id+"F0.wireOp",EDGE,"E5.MirrorCS"),sQuery(id+"F0.wireOp",EDGE,"E6.MirrorCS"),sQuery(id+"F0.wireOp",EDGE,"E7.filletArc"),sQuery(id+"F0.wireOp",EDGE,"E8.filletArc"),sQuery(id+"F0.wireOp",EDGE,"E9.filletArc"),sQuery(id+"F0.wireOp",EDGE,"E10.filletArc"),sQuery(id+"F0.wireOp",EDGE,"E11.filletArc"),sQuery(id+"F0.wireOp",EDGE,"E12.filletArc"),sQuery(id+"F0.wireOp",EDGE,"E13.1.0"),sQuery(id+"F0.wireOp",EDGE,"E13.1.1"),sQuery(id+"F0.wireOp",EDGE,"E13.1.2"),sQuery(id+"F0.wireOp",EDGE,"E13.1.3"),sQuery(id+"F0.wireOp",EDGE,"E13.1.4"),sQuery(id+"F0.wireOp",EDGE,"E13.1.5"),sQuery(id+"F0.wireOp",EDGE,"E13.1.6"),sQuery(id+"F0.wireOp",EDGE,"E13.1.7"),sQuery(id+"F0.wireOp",EDGE,"E13.1.8"),sQuery(id+"F0.wireOp",EDGE,"E13.1.9"),sQuery(id+"F0.wireOp",EDGE,"E13.1.10"),sQuery(id+"F0.wireOp",EDGE,"E13.1.11"),sQuery(id+"F0.wireOp",EDGE,"E13.2.0"),sQuery(id+"F0.wireOp",EDGE,"E13.2.1"),sQuery(id+"F0.wireOp",EDGE,"E13.2.2"),sQuery(id+"F0.wireOp",EDGE,"E13.2.3"),sQuery(id+"F0.wireOp",EDGE,"E13.2.4"),sQuery(id+"F0.wireOp",EDGE,"E13.2.5"),sQuery(id+"F0.wireOp",EDGE,"E13.2.6"),sQuery(id+"F0.wireOp",EDGE,"E13.2.7"),sQuery(id+"F0.wireOp",EDGE,"E13.2.8"),sQuery(id+"F0.wireOp",EDGE,"E13.2.9"),sQuery(id+"F0.wireOp",EDGE,"E13.2.10"),sQuery(id+"F0.wireOp",EDGE,"E13.2.11"),sQuery(id+"F0.wireOp",EDGE,"E13.3.0"),sQuery(id+"F0.wireOp",EDGE,"E13.3.1"),sQuery(id+"F0.wireOp",EDGE,"E13.3.2"),sQuery(id+"F0.wireOp",EDGE,"E13.3.3"),sQuery(id+"F0.wireOp",EDGE,"E13.3.4"),sQuery(id+"F0.wireOp",EDGE,"E13.3.5"),sQuery(id+"F0.wireOp",EDGE,"E13.3.6"),sQuery(id+"F0.wireOp",EDGE,"E13.3.7"),sQuery(id+"F0.wireOp",EDGE,"E13.3.8"),sQuery(id+"F0.wireOp",EDGE,"E13.3.9"),sQuery(id+"F0.wireOp",EDGE,"E13.3.10"),sQuery(id+"F0.wireOp",EDGE,"E13.3.11"),sQuery(id+"F0.wireOp",EDGE,"E13.4.0"),sQuery(id+"F0.wireOp",EDGE,"E13.4.1"),sQuery(id+"F0.wireOp",EDGE,"E13.4.2"),sQuery(id+"F0.wireOp",EDGE,"E13.4.3"),sQuery(id+"F0.wireOp",EDGE,"E13.4.4"),sQuery(id+"F0.wireOp",EDGE,"E13.4.5"),sQuery(id+"F0.wireOp",EDGE,"E13.4.6"),sQuery(id+"F0.wireOp",EDGE,"E13.4.7"),sQuery(id+"F0.wireOp",EDGE,"E13.4.8"),sQuery(id+"F0.wireOp",EDGE,"E13.4.9"),sQuery(id+"F0.wireOp",EDGE,"E13.4.10"),sQuery(id+"F0.wireOp",EDGE,"E13.4.11"),sQuery(id+"F0.wireOp",EDGE,"E13.5.0"),sQuery(id+"F0.wireOp",EDGE,"E13.5.1"),sQuery(id+"F0.wireOp",EDGE,"E13.5.2"),sQuery(id+"F0.wireOp",EDGE,"E13.5.3"),sQuery(id+"F0.wireOp",EDGE,"E13.5.4"),sQuery(id+"F0.wireOp",EDGE,"E13.5.5"),sQuery(id+"F0.wireOp",EDGE,"E13.5.6"),sQuery(id+"F0.wireOp",EDGE,"E13.5.7"),sQuery(id+"F0.wireOp",EDGE,"E13.5.8"),sQuery(id+"F0.wireOp",EDGE,"E13.5.9"),sQuery(id+"F0.wireOp",EDGE,"E13.5.10"),sQuery(id+"F0.wireOp",EDGE,"E13.5.11"),sQuery(id+"F0.wireOp",EDGE,"E13.6.0"),sQuery(id+"F0.wireOp",EDGE,"E13.6.1"),sQuery(id+"F0.wireOp",EDGE,"E13.6.2"),sQuery(id+"F0.wireOp",EDGE,"E13.6.3"),sQuery(id+"F0.wireOp",EDGE,"E13.6.4"),sQuery(id+"F0.wireOp",EDGE,"E13.6.5"),sQuery(id+"F0.wireOp",EDGE,"E13.6.6"),sQuery(id+"F0.wireOp",EDGE,"E13.6.7"),sQuery(id+"F0.wireOp",EDGE,"E13.6.8"),sQuery(id+"F0.wireOp",EDGE,"E13.6.9"),sQuery(id+"F0.wireOp",EDGE,"E13.6.10"),sQuery(id+"F0.wireOp",EDGE,"E13.6.11"),sQuery(id+"F0.wireOp",EDGE,"E13.7.0"),sQuery(id+"F0.wireOp",EDGE,"E13.7.1"),sQuery(id+"F0.wireOp",EDGE,"E13.7.2"),sQuery(id+"F0.wireOp",EDGE,"E13.7.3"),sQuery(id+"F0.wireOp",EDGE,"E13.7.4"),sQuery(id+"F0.wireOp",EDGE,"E13.7.5"),sQuery(id+"F0.wireOp",EDGE,"E13.7.6"),sQuery(id+"F0.wireOp",EDGE,"E13.7.7"),sQuery(id+"F0.wireOp",EDGE,"E13.7.8"),sQuery(id+"F0.wireOp",EDGE,"E13.7.9"),sQuery(id+"F0.wireOp",EDGE,"E13.7.10"),sQuery(id+"F0.wireOp",EDGE,"E13.7.11"),sQuery(id+"F0.wireOp",EDGE,"E13.8.0"),sQuery(id+"F0.wireOp",EDGE,"E13.8.1"),sQuery(id+"F0.wireOp",EDGE,"E13.8.2"),sQuery(id+"F0.wireOp",EDGE,"E13.8.3"),sQuery(id+"F0.wireOp",EDGE,"E13.8.4"),sQuery(id+"F0.wireOp",EDGE,"E13.8.5"),sQuery(id+"F0.wireOp",EDGE,"E13.8.6"),sQuery(id+"F0.wireOp",EDGE,"E13.8.7"),sQuery(id+"F0.wireOp",EDGE,"E13.8.8"),sQuery(id+"F0.wireOp",EDGE,"E13.8.9"),sQuery(id+"F0.wireOp",EDGE,"E13.8.10"),sQuery(id+"F0.wireOp",EDGE,"E13.8.11"),sQuery(id+"F0.wireOp",EDGE,"E13.9.0"),sQuery(id+"F0.wireOp",EDGE,"E13.9.1"),sQuery(id+"F0.wireOp",EDGE,"E13.9.2"),sQuery(id+"F0.wireOp",EDGE,"E13.9.3"),sQuery(id+"F0.wireOp",EDGE,"E13.9.4"),sQuery(id+"F0.wireOp",EDGE,"E13.9.5"),sQuery(id+"F0.wireOp",EDGE,"E13.9.6"),sQuery(id+"F0.wireOp",EDGE,"E13.9.7"),sQuery(id+"F0.wireOp",EDGE,"E13.9.8"),sQuery(id+"F0.wireOp",EDGE,"E13.9.9"),sQuery(id+"F0.wireOp",EDGE,"E13.9.10"),sQuery(id+"F0.wireOp",EDGE,"E13.9.11"),sQuery(id+"F0.wireOp",EDGE,"E13.10.0"),sQuery(id+"F0.wireOp",EDGE,"E13.10.1"),sQuery(id+"F0.wireOp",EDGE,"E13.10.2"),sQuery(id+"F0.wireOp",EDGE,"E13.10.3"),sQuery(id+"F0.wireOp",EDGE,"E13.10.4"),sQuery(id+"F0.wireOp",EDGE,"E13.10.5"),sQuery(id+"F0.wireOp",EDGE,"E13.10.6"),sQuery(id+"F0.wireOp",EDGE,"E13.10.7"),sQuery(id+"F0.wireOp",EDGE,"E13.10.8"),sQuery(id+"F0.wireOp",EDGE,"E13.10.9"),sQuery(id+"F0.wireOp",EDGE,"E13.10.10"),sQuery(id+"F0.wireOp",EDGE,"E13.10.11"),sQuery(id+"F0.wireOp",EDGE,"E13.11.0"),sQuery(id+"F0.wireOp",EDGE,"E13.11.1"),sQuery(id+"F0.wireOp",EDGE,"E13.11.2"),sQuery(id+"F0.wireOp",EDGE,"E13.11.3"),sQuery(id+"F0.wireOp",EDGE,"E13.11.4"),sQuery(id+"F0.wireOp",EDGE,"E13.11.5"),sQuery(id+"F0.wireOp",EDGE,"E13.11.6"),sQuery(id+"F0.wireOp",EDGE,"E13.11.7"),sQuery(id+"F0.wireOp",EDGE,"E13.11.8"),sQuery(id+"F0.wireOp",EDGE,"E13.11.9"),sQuery(id+"F0.wireOp",EDGE,"E13.11.10"),sQuery(id+"F0.wireOp",EDGE,"E13.11.11"),sQuery(id+"F0.wireOp",EDGE,"E13.12.0"),sQuery(id+"F0.wireOp",EDGE,"E13.12.1"),sQuery(id+"F0.wireOp",EDGE,"E13.12.2"),sQuery(id+"F0.wireOp",EDGE,"E13.12.3"),sQuery(id+"F0.wireOp",EDGE,"E13.12.4"),sQuery(id+"F0.wireOp",EDGE,"E13.12.5"),sQuery(id+"F0.wireOp",EDGE,"E13.12.6"),sQuery(id+"F0.wireOp",EDGE,"E13.12.7"),sQuery(id+"F0.wireOp",EDGE,"E13.12.8"),sQuery(id+"F0.wireOp",EDGE,"E13.12.9"),sQuery(id+"F0.wireOp",EDGE,"E13.12.10"),sQuery(id+"F0.wireOp",EDGE,"E13.12.11"),sQuery(id+"F0.wireOp",EDGE,"E13.13.0"),sQuery(id+"F0.wireOp",EDGE,"E13.13.1"),sQuery(id+"F0.wireOp",EDGE,"E13.13.2"),sQuery(id+"F0.wireOp",EDGE,"E13.13.3"),sQuery(id+"F0.wireOp",EDGE,"E13.13.4"),sQuery(id+"F0.wireOp",EDGE,"E13.13.5"),sQuery(id+"F0.wireOp",EDGE,"E13.13.6"),sQuery(id+"F0.wireOp",EDGE,"E13.13.7"),sQuery(id+"F0.wireOp",EDGE,"E13.13.8"),sQuery(id+"F0.wireOp",EDGE,"E13.13.9"),sQuery(id+"F0.wireOp",EDGE,"E13.13.10"),sQuery(id+"F0.wireOp",EDGE,"E13.13.11"),sQuery(id+"F0.wireOp",EDGE,"E13.14.0"),sQuery(id+"F0.wireOp",EDGE,"E13.14.1"),sQuery(id+"F0.wireOp",EDGE,"E13.14.2"),sQuery(id+"F0.wireOp",EDGE,"E13.14.3"),sQuery(id+"F0.wireOp",EDGE,"E13.14.4"),sQuery(id+"F0.wireOp",EDGE,"E13.14.5"),sQuery(id+"F0.wireOp",EDGE,"E13.14.6"),sQuery(id+"F0.wireOp",EDGE,"E13.14.7"),sQuery(id+"F0.wireOp",EDGE,"E13.14.8"),sQuery(id+"F0.wireOp",EDGE,"E13.14.9"),sQuery(id+"F0.wireOp",EDGE,"E13.14.10"),sQuery(id+"F0.wireOp",EDGE,"E13.14.11"),sQuery(id+"F0.wireOp",EDGE,"E13.15.0"),sQuery(id+"F0.wireOp",EDGE,"E13.15.1"),sQuery(id+"F0.wireOp",EDGE,"E13.15.2"),sQuery(id+"F0.wireOp",EDGE,"E13.15.3"),sQuery(id+"F0.wireOp",EDGE,"E13.15.4"),sQuery(id+"F0.wireOp",EDGE,"E13.15.5"),sQuery(id+"F0.wireOp",EDGE,"E13.15.6"),sQuery(id+"F0.wireOp",EDGE,"E13.15.7"),sQuery(id+"F0.wireOp",EDGE,"E13.15.8"),sQuery(id+"F0.wireOp",EDGE,"E13.15.9"),sQuery(id+"F0.wireOp",EDGE,"E13.15.10"),sQuery(id+"F0.wireOp",EDGE,"E13.15.11"),sQuery(id+"F0.wireOp",EDGE,"E13.16.0"),sQuery(id+"F0.wireOp",EDGE,"E13.16.1"),sQuery(id+"F0.wireOp",EDGE,"E13.16.2"),sQuery(id+"F0.wireOp",EDGE,"E13.16.3"),sQuery(id+"F0.wireOp",EDGE,"E13.16.4"),sQuery(id+"F0.wireOp",EDGE,"E13.16.5"),sQuery(id+"F0.wireOp",EDGE,"E13.16.6"),sQuery(id+"F0.wireOp",EDGE,"E13.16.7"),sQuery(id+"F0.wireOp",EDGE,"E13.16.8"),sQuery(id+"F0.wireOp",EDGE,"E13.16.9"),sQuery(id+"F0.wireOp",EDGE,"E13.16.10"),sQuery(id+"F0.wireOp",EDGE,"E13.16.11"),sQuery(id+"F0.wireOp",EDGE,"E13.17.0"),sQuery(id+"F0.wireOp",EDGE,"E13.17.1"),sQuery(id+"F0.wireOp",EDGE,"E13.17.2"),sQuery(id+"F0.wireOp",EDGE,"E13.17.3"),sQuery(id+"F0.wireOp",EDGE,"E13.17.4"),sQuery(id+"F0.wireOp",EDGE,"E13.17.5"),sQuery(id+"F0.wireOp",EDGE,"E13.17.6"),sQuery(id+"F0.wireOp",EDGE,"E13.17.7"),sQuery(id+"F0.wireOp",EDGE,"E13.17.8"),sQuery(id+"F0.wireOp",EDGE,"E13.17.9"),sQuery(id+"F0.wireOp",EDGE,"E13.17.10"),sQuery(id+"F0.wireOp",EDGE,"E13.17.11"),sQuery(id+"F0.wireOp",EDGE,"E14.trimOffspring"),sQuery(id+"F0.wireOp",EDGE,"E15.trimOffspring"),sQuery(id+"F0.wireOp",EDGE,"E16.trimOffspring"),sQuery(id+"F0.wireOp",EDGE,"E17.trimOffspring"),sQuery(id+"F0.wireOp",EDGE,"E18.trimOffspring"),sQuery(id+"F0.wireOp",EDGE,"E19.trimOffspring"),sQuery(id+"F0.wireOp",EDGE,"E20.trimOffspring"),sQuery(id+"F0.wireOp",EDGE,"E21.trimOffspring"),sQuery(id+"F0.wireOp",EDGE,"E22.trimOffspring"),sQuery(id+"F0.wireOp",EDGE,"E23.trimOffspring"),sQuery(id+"F0.wireOp",EDGE,"E24.trimOffspring"),sQuery(id+"F0.wireOp",EDGE,"E25.trimOffspring"),sQuery(id+"F0.wireOp",EDGE,"E26.trimOffspring"),sQuery(id+"F0.wireOp",EDGE,"E27.trimOffspring"),sQuery(id+"F0.wireOp",EDGE,"E28.trimOffspring"),sQuery(id+"F0.wireOp",EDGE,"E29.trimOffspring"),sQuery(id+"F0.wireOp",EDGE,"E30.trimOffspring")])],"isStart":false});
            var sketch = newSketch(context, id + "F2", { "sketchPlane" : qUnion([Q0])});
            skCircle(sketch, "E31", {"center": v(0, 0) * mm, "radius": 3.18 * mm});
            skSolve(sketch);
        }
        {
            var Q0;
            Q0 = qSketchRegion(id + "F2", true);
            extrude(context, id + "F3", {"entities" : qUnion([Q0]), "operationType" : NewBodyOperationType.REMOVE, "oppositeDirection" : true, "depth" : 25.4 * mm});
        }
        {
            var Q0;
            Q0=makeQuery(id+"F1.opExtrude","CAP_FACE",FACE,{"disambiguationData":[OSD([sQuery(id+"F0.wireOp",EDGE,"E0"),sQuery(id+"F0.wireOp",EDGE,"E1.trimOffspring"),sQuery(id+"F0.wireOp",EDGE,"E2"),sQuery(id+"F0.wireOp",EDGE,"E3"),sQuery(id+"F0.wireOp",EDGE,"E4.MirrorCS"),sQuery(id+"F0.wireOp",EDGE,"E5.MirrorCS"),sQuery(id+"F0.wireOp",EDGE,"E6.MirrorCS"),sQuery(id+"F0.wireOp",EDGE,"E7.filletArc"),sQuery(id+"F0.wireOp",EDGE,"E8.filletArc"),sQuery(id+"F0.wireOp",EDGE,"E9.filletArc"),sQuery(id+"F0.wireOp",EDGE,"E10.filletArc"),sQuery(id+"F0.wireOp",EDGE,"E11.filletArc"),sQuery(id+"F0.wireOp",EDGE,"E12.filletArc"),sQuery(id+"F0.wireOp",EDGE,"E13.1.0"),sQuery(id+"F0.wireOp",EDGE,"E13.1.1"),sQuery(id+"F0.wireOp",EDGE,"E13.1.2"),sQuery(id+"F0.wireOp",EDGE,"E13.1.3"),sQuery(id+"F0.wireOp",EDGE,"E13.1.4"),sQuery(id+"F0.wireOp",EDGE,"E13.1.5"),sQuery(id+"F0.wireOp",EDGE,"E13.1.6"),sQuery(id+"F0.wireOp",EDGE,"E13.1.7"),sQuery(id+"F0.wireOp",EDGE,"E13.1.8"),sQuery(id+"F0.wireOp",EDGE,"E13.1.9"),sQuery(id+"F0.wireOp",EDGE,"E13.1.10"),sQuery(id+"F0.wireOp",EDGE,"E13.1.11"),sQuery(id+"F0.wireOp",EDGE,"E13.2.0"),sQuery(id+"F0.wireOp",EDGE,"E13.2.1"),sQuery(id+"F0.wireOp",EDGE,"E13.2.2"),sQuery(id+"F0.wireOp",EDGE,"E13.2.3"),sQuery(id+"F0.wireOp",EDGE,"E13.2.4"),sQuery(id+"F0.wireOp",EDGE,"E13.2.5"),sQuery(id+"F0.wireOp",EDGE,"E13.2.6"),sQuery(id+"F0.wireOp",EDGE,"E13.2.7"),sQuery(id+"F0.wireOp",EDGE,"E13.2.8"),sQuery(id+"F0.wireOp",EDGE,"E13.2.9"),sQuery(id+"F0.wireOp",EDGE,"E13.2.10"),sQuery(id+"F0.wireOp",EDGE,"E13.2.11"),sQuery(id+"F0.wireOp",EDGE,"E13.3.0"),sQuery(id+"F0.wireOp",EDGE,"E13.3.1"),sQuery(id+"F0.wireOp",EDGE,"E13.3.2"),sQuery(id+"F0.wireOp",EDGE,"E13.3.3"),sQuery(id+"F0.wireOp",EDGE,"E13.3.4"),sQuery(id+"F0.wireOp",EDGE,"E13.3.5"),sQuery(id+"F0.wireOp",EDGE,"E13.3.6"),sQuery(id+"F0.wireOp",EDGE,"E13.3.7"),sQuery(id+"F0.wireOp",EDGE,"E13.3.8"),sQuery(id+"F0.wireOp",EDGE,"E13.3.9"),sQuery(id+"F0.wireOp",EDGE,"E13.3.10"),sQuery(id+"F0.wireOp",EDGE,"E13.3.11"),sQuery(id+"F0.wireOp",EDGE,"E13.4.0"),sQuery(id+"F0.wireOp",EDGE,"E13.4.1"),sQuery(id+"F0.wireOp",EDGE,"E13.4.2"),sQuery(id+"F0.wireOp",EDGE,"E13.4.3"),sQuery(id+"F0.wireOp",EDGE,"E13.4.4"),sQuery(id+"F0.wireOp",EDGE,"E13.4.5"),sQuery(id+"F0.wireOp",EDGE,"E13.4.6"),sQuery(id+"F0.wireOp",EDGE,"E13.4.7"),sQuery(id+"F0.wireOp",EDGE,"E13.4.8"),sQuery(id+"F0.wireOp",EDGE,"E13.4.9"),sQuery(id+"F0.wireOp",EDGE,"E13.4.10"),sQuery(id+"F0.wireOp",EDGE,"E13.4.11"),sQuery(id+"F0.wireOp",EDGE,"E13.5.0"),sQuery(id+"F0.wireOp",EDGE,"E13.5.1"),sQuery(id+"F0.wireOp",EDGE,"E13.5.2"),sQuery(id+"F0.wireOp",EDGE,"E13.5.3"),sQuery(id+"F0.wireOp",EDGE,"E13.5.4"),sQuery(id+"F0.wireOp",EDGE,"E13.5.5"),sQuery(id+"F0.wireOp",EDGE,"E13.5.6"),sQuery(id+"F0.wireOp",EDGE,"E13.5.7"),sQuery(id+"F0.wireOp",EDGE,"E13.5.8"),sQuery(id+"F0.wireOp",EDGE,"E13.5.9"),sQuery(id+"F0.wireOp",EDGE,"E13.5.10"),sQuery(id+"F0.wireOp",EDGE,"E13.5.11"),sQuery(id+"F0.wireOp",EDGE,"E13.6.0"),sQuery(id+"F0.wireOp",EDGE,"E13.6.1"),sQuery(id+"F0.wireOp",EDGE,"E13.6.2"),sQuery(id+"F0.wireOp",EDGE,"E13.6.3"),sQuery(id+"F0.wireOp",EDGE,"E13.6.4"),sQuery(id+"F0.wireOp",EDGE,"E13.6.5"),sQuery(id+"F0.wireOp",EDGE,"E13.6.6"),sQuery(id+"F0.wireOp",EDGE,"E13.6.7"),sQuery(id+"F0.wireOp",EDGE,"E13.6.8"),sQuery(id+"F0.wireOp",EDGE,"E13.6.9"),sQuery(id+"F0.wireOp",EDGE,"E13.6.10"),sQuery(id+"F0.wireOp",EDGE,"E13.6.11"),sQuery(id+"F0.wireOp",EDGE,"E13.7.0"),sQuery(id+"F0.wireOp",EDGE,"E13.7.1"),sQuery(id+"F0.wireOp",EDGE,"E13.7.2"),sQuery(id+"F0.wireOp",EDGE,"E13.7.3"),sQuery(id+"F0.wireOp",EDGE,"E13.7.4"),sQuery(id+"F0.wireOp",EDGE,"E13.7.5"),sQuery(id+"F0.wireOp",EDGE,"E13.7.6"),sQuery(id+"F0.wireOp",EDGE,"E13.7.7"),sQuery(id+"F0.wireOp",EDGE,"E13.7.8"),sQuery(id+"F0.wireOp",EDGE,"E13.7.9"),sQuery(id+"F0.wireOp",EDGE,"E13.7.10"),sQuery(id+"F0.wireOp",EDGE,"E13.7.11"),sQuery(id+"F0.wireOp",EDGE,"E13.8.0"),sQuery(id+"F0.wireOp",EDGE,"E13.8.1"),sQuery(id+"F0.wireOp",EDGE,"E13.8.2"),sQuery(id+"F0.wireOp",EDGE,"E13.8.3"),sQuery(id+"F0.wireOp",EDGE,"E13.8.4"),sQuery(id+"F0.wireOp",EDGE,"E13.8.5"),sQuery(id+"F0.wireOp",EDGE,"E13.8.6"),sQuery(id+"F0.wireOp",EDGE,"E13.8.7"),sQuery(id+"F0.wireOp",EDGE,"E13.8.8"),sQuery(id+"F0.wireOp",EDGE,"E13.8.9"),sQuery(id+"F0.wireOp",EDGE,"E13.8.10"),sQuery(id+"F0.wireOp",EDGE,"E13.8.11"),sQuery(id+"F0.wireOp",EDGE,"E13.9.0"),sQuery(id+"F0.wireOp",EDGE,"E13.9.1"),sQuery(id+"F0.wireOp",EDGE,"E13.9.2"),sQuery(id+"F0.wireOp",EDGE,"E13.9.3"),sQuery(id+"F0.wireOp",EDGE,"E13.9.4"),sQuery(id+"F0.wireOp",EDGE,"E13.9.5"),sQuery(id+"F0.wireOp",EDGE,"E13.9.6"),sQuery(id+"F0.wireOp",EDGE,"E13.9.7"),sQuery(id+"F0.wireOp",EDGE,"E13.9.8"),sQuery(id+"F0.wireOp",EDGE,"E13.9.9"),sQuery(id+"F0.wireOp",EDGE,"E13.9.10"),sQuery(id+"F0.wireOp",EDGE,"E13.9.11"),sQuery(id+"F0.wireOp",EDGE,"E13.10.0"),sQuery(id+"F0.wireOp",EDGE,"E13.10.1"),sQuery(id+"F0.wireOp",EDGE,"E13.10.2"),sQuery(id+"F0.wireOp",EDGE,"E13.10.3"),sQuery(id+"F0.wireOp",EDGE,"E13.10.4"),sQuery(id+"F0.wireOp",EDGE,"E13.10.5"),sQuery(id+"F0.wireOp",EDGE,"E13.10.6"),sQuery(id+"F0.wireOp",EDGE,"E13.10.7"),sQuery(id+"F0.wireOp",EDGE,"E13.10.8"),sQuery(id+"F0.wireOp",EDGE,"E13.10.9"),sQuery(id+"F0.wireOp",EDGE,"E13.10.10"),sQuery(id+"F0.wireOp",EDGE,"E13.10.11"),sQuery(id+"F0.wireOp",EDGE,"E13.11.0"),sQuery(id+"F0.wireOp",EDGE,"E13.11.1"),sQuery(id+"F0.wireOp",EDGE,"E13.11.2"),sQuery(id+"F0.wireOp",EDGE,"E13.11.3"),sQuery(id+"F0.wireOp",EDGE,"E13.11.4"),sQuery(id+"F0.wireOp",EDGE,"E13.11.5"),sQuery(id+"F0.wireOp",EDGE,"E13.11.6"),sQuery(id+"F0.wireOp",EDGE,"E13.11.7"),sQuery(id+"F0.wireOp",EDGE,"E13.11.8"),sQuery(id+"F0.wireOp",EDGE,"E13.11.9"),sQuery(id+"F0.wireOp",EDGE,"E13.11.10"),sQuery(id+"F0.wireOp",EDGE,"E13.11.11"),sQuery(id+"F0.wireOp",EDGE,"E13.12.0"),sQuery(id+"F0.wireOp",EDGE,"E13.12.1"),sQuery(id+"F0.wireOp",EDGE,"E13.12.2"),sQuery(id+"F0.wireOp",EDGE,"E13.12.3"),sQuery(id+"F0.wireOp",EDGE,"E13.12.4"),sQuery(id+"F0.wireOp",EDGE,"E13.12.5"),sQuery(id+"F0.wireOp",EDGE,"E13.12.6"),sQuery(id+"F0.wireOp",EDGE,"E13.12.7"),sQuery(id+"F0.wireOp",EDGE,"E13.12.8"),sQuery(id+"F0.wireOp",EDGE,"E13.12.9"),sQuery(id+"F0.wireOp",EDGE,"E13.12.10"),sQuery(id+"F0.wireOp",EDGE,"E13.12.11"),sQuery(id+"F0.wireOp",EDGE,"E13.13.0"),sQuery(id+"F0.wireOp",EDGE,"E13.13.1"),sQuery(id+"F0.wireOp",EDGE,"E13.13.2"),sQuery(id+"F0.wireOp",EDGE,"E13.13.3"),sQuery(id+"F0.wireOp",EDGE,"E13.13.4"),sQuery(id+"F0.wireOp",EDGE,"E13.13.5"),sQuery(id+"F0.wireOp",EDGE,"E13.13.6"),sQuery(id+"F0.wireOp",EDGE,"E13.13.7"),sQuery(id+"F0.wireOp",EDGE,"E13.13.8"),sQuery(id+"F0.wireOp",EDGE,"E13.13.9"),sQuery(id+"F0.wireOp",EDGE,"E13.13.10"),sQuery(id+"F0.wireOp",EDGE,"E13.13.11"),sQuery(id+"F0.wireOp",EDGE,"E13.14.0"),sQuery(id+"F0.wireOp",EDGE,"E13.14.1"),sQuery(id+"F0.wireOp",EDGE,"E13.14.2"),sQuery(id+"F0.wireOp",EDGE,"E13.14.3"),sQuery(id+"F0.wireOp",EDGE,"E13.14.4"),sQuery(id+"F0.wireOp",EDGE,"E13.14.5"),sQuery(id+"F0.wireOp",EDGE,"E13.14.6"),sQuery(id+"F0.wireOp",EDGE,"E13.14.7"),sQuery(id+"F0.wireOp",EDGE,"E13.14.8"),sQuery(id+"F0.wireOp",EDGE,"E13.14.9"),sQuery(id+"F0.wireOp",EDGE,"E13.14.10"),sQuery(id+"F0.wireOp",EDGE,"E13.14.11"),sQuery(id+"F0.wireOp",EDGE,"E13.15.0"),sQuery(id+"F0.wireOp",EDGE,"E13.15.1"),sQuery(id+"F0.wireOp",EDGE,"E13.15.2"),sQuery(id+"F0.wireOp",EDGE,"E13.15.3"),sQuery(id+"F0.wireOp",EDGE,"E13.15.4"),sQuery(id+"F0.wireOp",EDGE,"E13.15.5"),sQuery(id+"F0.wireOp",EDGE,"E13.15.6"),sQuery(id+"F0.wireOp",EDGE,"E13.15.7"),sQuery(id+"F0.wireOp",EDGE,"E13.15.8"),sQuery(id+"F0.wireOp",EDGE,"E13.15.9"),sQuery(id+"F0.wireOp",EDGE,"E13.15.10"),sQuery(id+"F0.wireOp",EDGE,"E13.15.11"),sQuery(id+"F0.wireOp",EDGE,"E13.16.0"),sQuery(id+"F0.wireOp",EDGE,"E13.16.1"),sQuery(id+"F0.wireOp",EDGE,"E13.16.2"),sQuery(id+"F0.wireOp",EDGE,"E13.16.3"),sQuery(id+"F0.wireOp",EDGE,"E13.16.4"),sQuery(id+"F0.wireOp",EDGE,"E13.16.5"),sQuery(id+"F0.wireOp",EDGE,"E13.16.6"),sQuery(id+"F0.wireOp",EDGE,"E13.16.7"),sQuery(id+"F0.wireOp",EDGE,"E13.16.8"),sQuery(id+"F0.wireOp",EDGE,"E13.16.9"),sQuery(id+"F0.wireOp",EDGE,"E13.16.10"),sQuery(id+"F0.wireOp",EDGE,"E13.16.11"),sQuery(id+"F0.wireOp",EDGE,"E13.17.0"),sQuery(id+"F0.wireOp",EDGE,"E13.17.1"),sQuery(id+"F0.wireOp",EDGE,"E13.17.2"),sQuery(id+"F0.wireOp",EDGE,"E13.17.3"),sQuery(id+"F0.wireOp",EDGE,"E13.17.4"),sQuery(id+"F0.wireOp",EDGE,"E13.17.5"),sQuery(id+"F0.wireOp",EDGE,"E13.17.6"),sQuery(id+"F0.wireOp",EDGE,"E13.17.7"),sQuery(id+"F0.wireOp",EDGE,"E13.17.8"),sQuery(id+"F0.wireOp",EDGE,"E13.17.9"),sQuery(id+"F0.wireOp",EDGE,"E13.17.10"),sQuery(id+"F0.wireOp",EDGE,"E13.17.11"),sQuery(id+"F0.wireOp",EDGE,"E14.trimOffspring"),sQuery(id+"F0.wireOp",EDGE,"E15.trimOffspring"),sQuery(id+"F0.wireOp",EDGE,"E16.trimOffspring"),sQuery(id+"F0.wireOp",EDGE,"E17.trimOffspring"),sQuery(id+"F0.wireOp",EDGE,"E18.trimOffspring"),sQuery(id+"F0.wireOp",EDGE,"E19.trimOffspring"),sQuery(id+"F0.wireOp",EDGE,"E20.trimOffspring"),sQuery(id+"F0.wireOp",EDGE,"E21.trimOffspring"),sQuery(id+"F0.wireOp",EDGE,"E22.trimOffspring"),sQuery(id+"F0.wireOp",EDGE,"E23.trimOffspring"),sQuery(id+"F0.wireOp",EDGE,"E24.trimOffspring"),sQuery(id+"F0.wireOp",EDGE,"E25.trimOffspring"),sQuery(id+"F0.wireOp",EDGE,"E26.trimOffspring"),sQuery(id+"F0.wireOp",EDGE,"E27.trimOffspring"),sQuery(id+"F0.wireOp",EDGE,"E28.trimOffspring"),sQuery(id+"F0.wireOp",EDGE,"E29.trimOffspring"),sQuery(id+"F0.wireOp",EDGE,"E30.trimOffspring")])],"isStart":false});
            shell(context, id + "F4", {"entities" : qUnion([Q0]), "thickness" : 5.08 * mm});
        }
        {
            var Q0;
            Q0=qCreatedBy(makeId("Right.planeOp"),FACE);
            cPlane(context, id + "F5", {"entities" : qUnion([Q0]), "cplaneType" : CPlaneType.OFFSET, "offset" : 8.25 * mm, "width" : 152.4 * mm, "height" : 152.4 * mm});
        }
        {
            var Q0;
            Q0=qCreatedBy(id+"F5.planeOp",FACE);
            var sketch = newSketch(context, id + "F6", { "sketchPlane" : qUnion([Q0])});
            skCircle(sketch, "E32", {"center": v(-9.53, 0) * mm, "radius": 1.13 * mm});
            skSolve(sketch);
        }
        {
            var Q0;
            Q0 = qSketchRegion(id + "F6", true);
            extrude(context, id + "F7", {"entities" : qUnion([Q0]), "operationType" : NewBodyOperationType.REMOVE, "oppositeDirection" : true, "depth" : 8.25 * mm});
        }
    });
